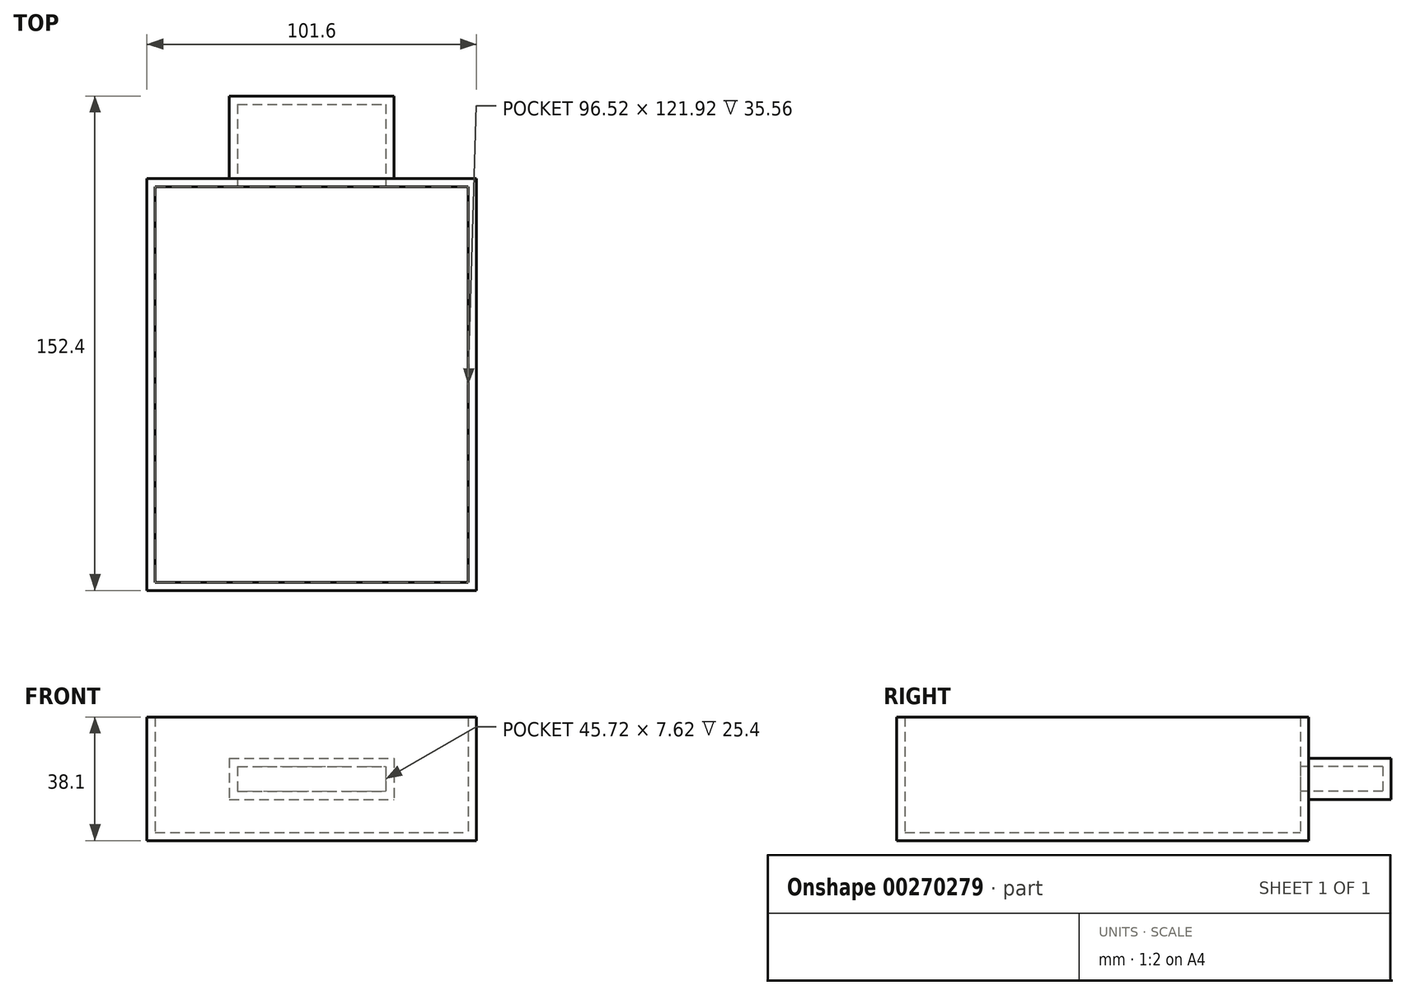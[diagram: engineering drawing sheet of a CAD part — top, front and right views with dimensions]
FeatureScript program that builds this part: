
annotation { "Feature Type Name" : "Feature", "Feature Type Description" : "" }
export const myFeature = defineFeature(function(context is Context, id is Id, definition is map)
    precondition{}
    {
        {
            var Q0;
            Q0=qCreatedBy(makeId("Front.planeOp"),FACE);
            var sketch = newSketch(context, id + "F0", { "sketchPlane" : qUnion([Q0])});
            skLineSegment(sketch, "E0.bottom", {"start": v(-50.8, 19.05) * mm, "end": v(50.8, 19.05) * mm});
            skLineSegment(sketch, "E0.top", {"start": v(-50.8, -19.05) * mm, "end": v(50.8, -19.05) * mm});
            skLineSegment(sketch, "E0.left", {"start": v(-50.8, 19.05) * mm, "end": v(-50.8, -19.05) * mm});
            skLineSegment(sketch, "E0.right", {"start": v(50.8, 19.05) * mm, "end": v(50.8, -19.05) * mm});
            skPoint(sketch, "E0.middle", {"position": v(0, 0) * mm});
            skSolve(sketch);
        }
        {
            var Q0;
            Q0 = qSketchRegion(id + "F0", true);
            extrude(context, id + "F1", {"entities" : qUnion([Q0]), "depth" : 127 * mm});
        }
        {
            var Q0;
            Q0=qCreatedBy(makeId("Front.planeOp"),FACE);
            var sketch = newSketch(context, id + "F2", { "sketchPlane" : qUnion([Q0])});
            skLineSegment(sketch, "E1.bottom", {"start": v(-25.4, 6.35) * mm, "end": v(25.4, 6.35) * mm});
            skLineSegment(sketch, "E1.top", {"start": v(-25.4, -6.35) * mm, "end": v(25.4, -6.35) * mm});
            skLineSegment(sketch, "E1.left", {"start": v(-25.4, 6.35) * mm, "end": v(-25.4, -6.35) * mm});
            skLineSegment(sketch, "E1.right", {"start": v(25.4, 6.35) * mm, "end": v(25.4, -6.35) * mm});
            skPoint(sketch, "E1.middle", {"position": v(0, 0) * mm});
            skSolve(sketch);
        }
        {
            var Q0;
            Q0 = qSketchRegion(id + "F2", true);
            var Q1;
            Q1=makeQuery(id+"F1.opExtrude","CAP_FACE",FACE,{"disambiguationData":[OSD([sQuery(id+"F0.wireOp",EDGE,"E0.bottom"),sQuery(id+"F0.wireOp",EDGE,"E0.top"),sQuery(id+"F0.wireOp",EDGE,"E0.left"),sQuery(id+"F0.wireOp",EDGE,"E0.right")])],"isStart":false});
            extrude(context, id + "F3", {"entities" : qUnion([Q0, Q1]), "operationType" : NewBodyOperationType.ADD, "oppositeDirection" : true, "depth" : 25.4 * mm});
        }
        {
            var Q0;
            Q0=makeQuery(id+"F1.opExtrude","SWEPT_FACE",FACE,{"disambiguationData":[OSD([sQuery(id+"F0.wireOp",EDGE,"E0.bottom")])]});
            shell(context, id + "F4", {"entities" : qUnion([Q0]), "thickness" : 2.54 * mm});
        }
    });
